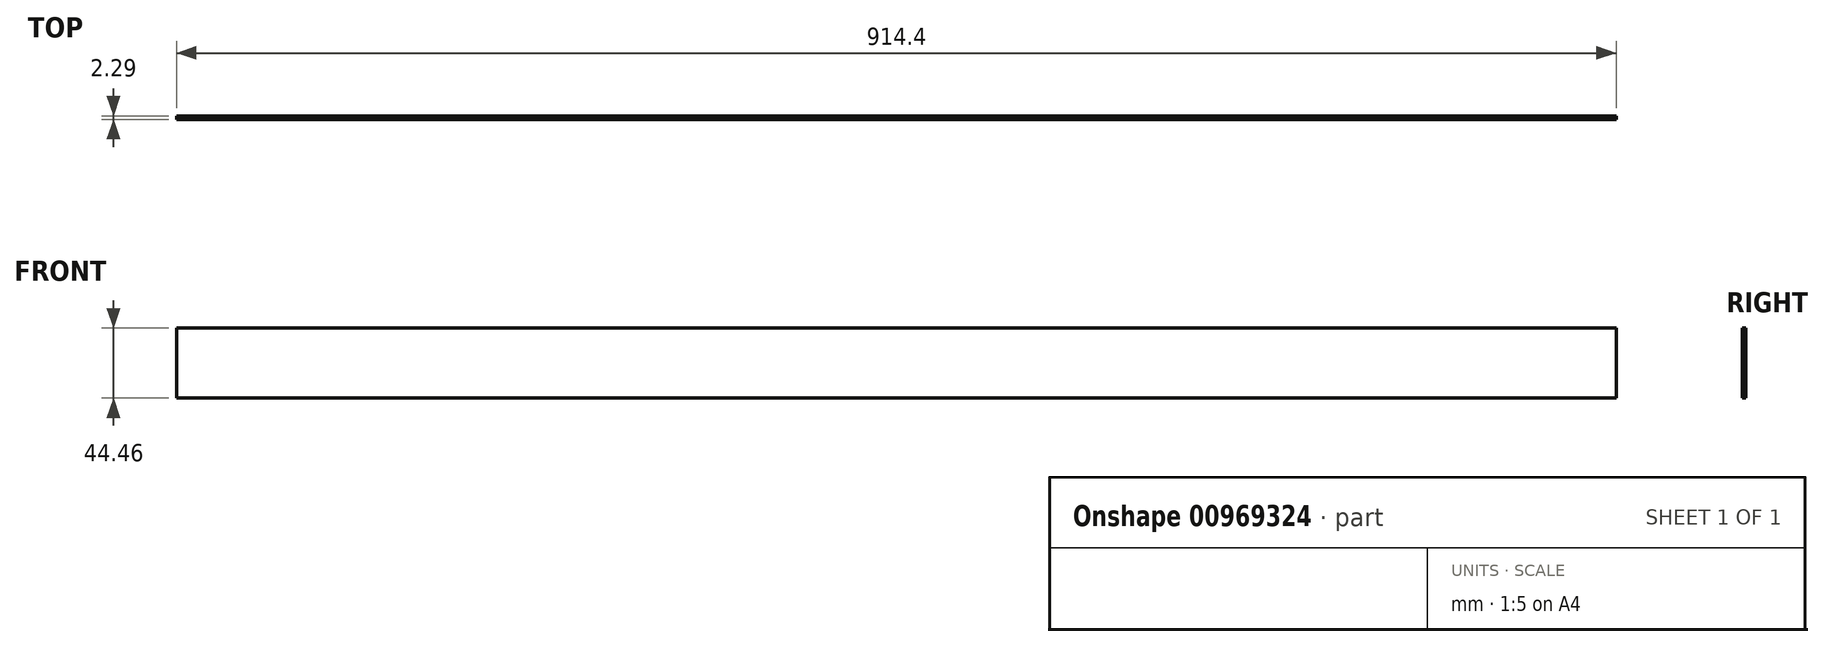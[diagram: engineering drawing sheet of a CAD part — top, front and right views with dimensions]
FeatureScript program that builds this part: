
annotation { "Feature Type Name" : "Feature", "Feature Type Description" : "" }
export const myFeature = defineFeature(function(context is Context, id is Id, definition is map)
    precondition{}
    {
        {
            var Q0;
            Q0=qCreatedBy(makeId("Front.planeOp"),FACE);
            var sketch = newSketch(context, id + "F0", { "sketchPlane" : qUnion([Q0])});
            skLineSegment(sketch, "E0.bottom", {"start": v(457.2, -22.22) * mm, "end": v(-457.2, -22.23) * mm});
            skLineSegment(sketch, "E0.top", {"start": v(457.2, 22.23) * mm, "end": v(-457.2, 22.22) * mm});
            skLineSegment(sketch, "E0.left", {"start": v(457.2, -22.22) * mm, "end": v(457.2, 22.23) * mm});
            skLineSegment(sketch, "E0.right", {"start": v(-457.2, -22.23) * mm, "end": v(-457.2, 22.22) * mm});
            skPoint(sketch, "E0.middle", {"position": v(0, 0) * mm});
            skSolve(sketch);
        }
        {
            var Q0;
            Q0 = qSketchRegion(id + "F0", true);
            extrude(context, id + "F1", {"entities" : qUnion([Q0]), "depth" : 2.3 * mm, "offsetDistance" : 25.4 * mm});
        }
    });
